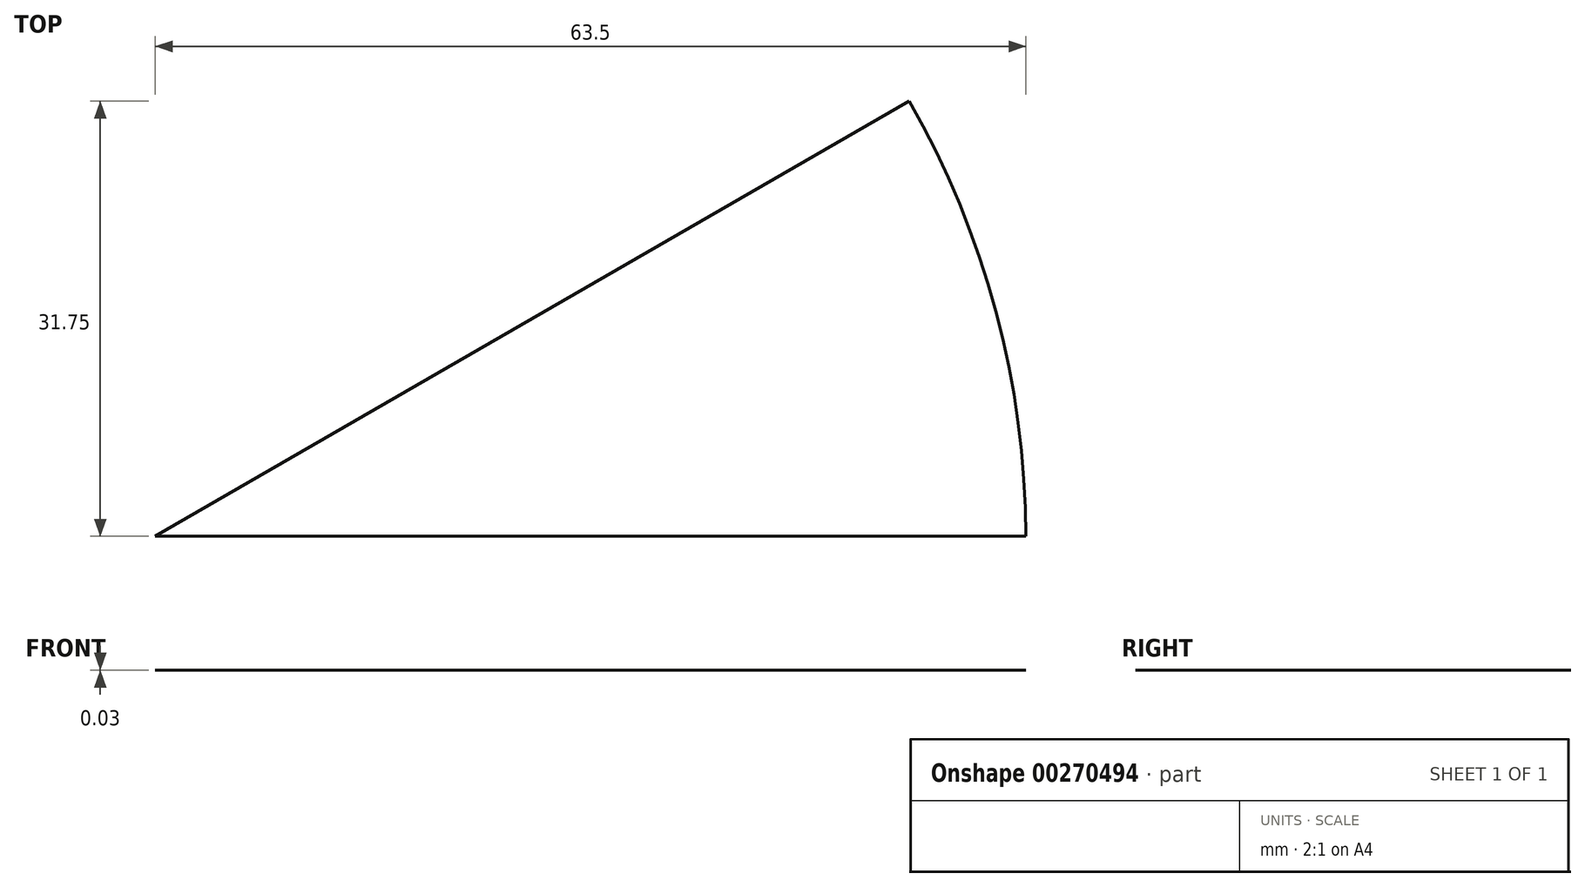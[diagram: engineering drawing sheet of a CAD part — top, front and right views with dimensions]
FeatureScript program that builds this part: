
annotation { "Feature Type Name" : "Feature", "Feature Type Description" : "" }
export const myFeature = defineFeature(function(context is Context, id is Id, definition is map)
    precondition{}
    {
        {
            var Q0;
            Q0=qCreatedBy(makeId("Top.planeOp"),FACE);
            var sketch = newSketch(context, id + "F0", { "sketchPlane" : qUnion([Q0])});
            skPoint(sketch, "E0.center", {"position": v(0, 0) * mm});
            skLineSegment(sketch, "E1", {"start": v(0, 0) * mm, "end": v(55, 31.75) * mm});
            skLineSegment(sketch, "E2", {"start": v(0, 0) * mm, "end": v(63.5, 0) * mm});
            skArc(sketch, "E3", {"start": v(63.5, 0) * mm, "mid": v(61.3, 16.43) * mm, "end": v(55, 31.75) * mm});
            skSolve(sketch);
        }
        {
            var Q0;
            Q0=makeQuery(id+"F0.imprint","IMPRINT",FACE,{"disambiguationData":[TD([[makeQuery(id+"F0.imprint","IMPRINT",EDGE,{"derivedFrom":sQuery(id+"F0.wireOp",EDGE,"E1")}),-1.0]])]});
            extrude(context, id + "F1", {"entities" : qUnion([Q0]), "depth" : 0.03 * mm});
        }
    });
